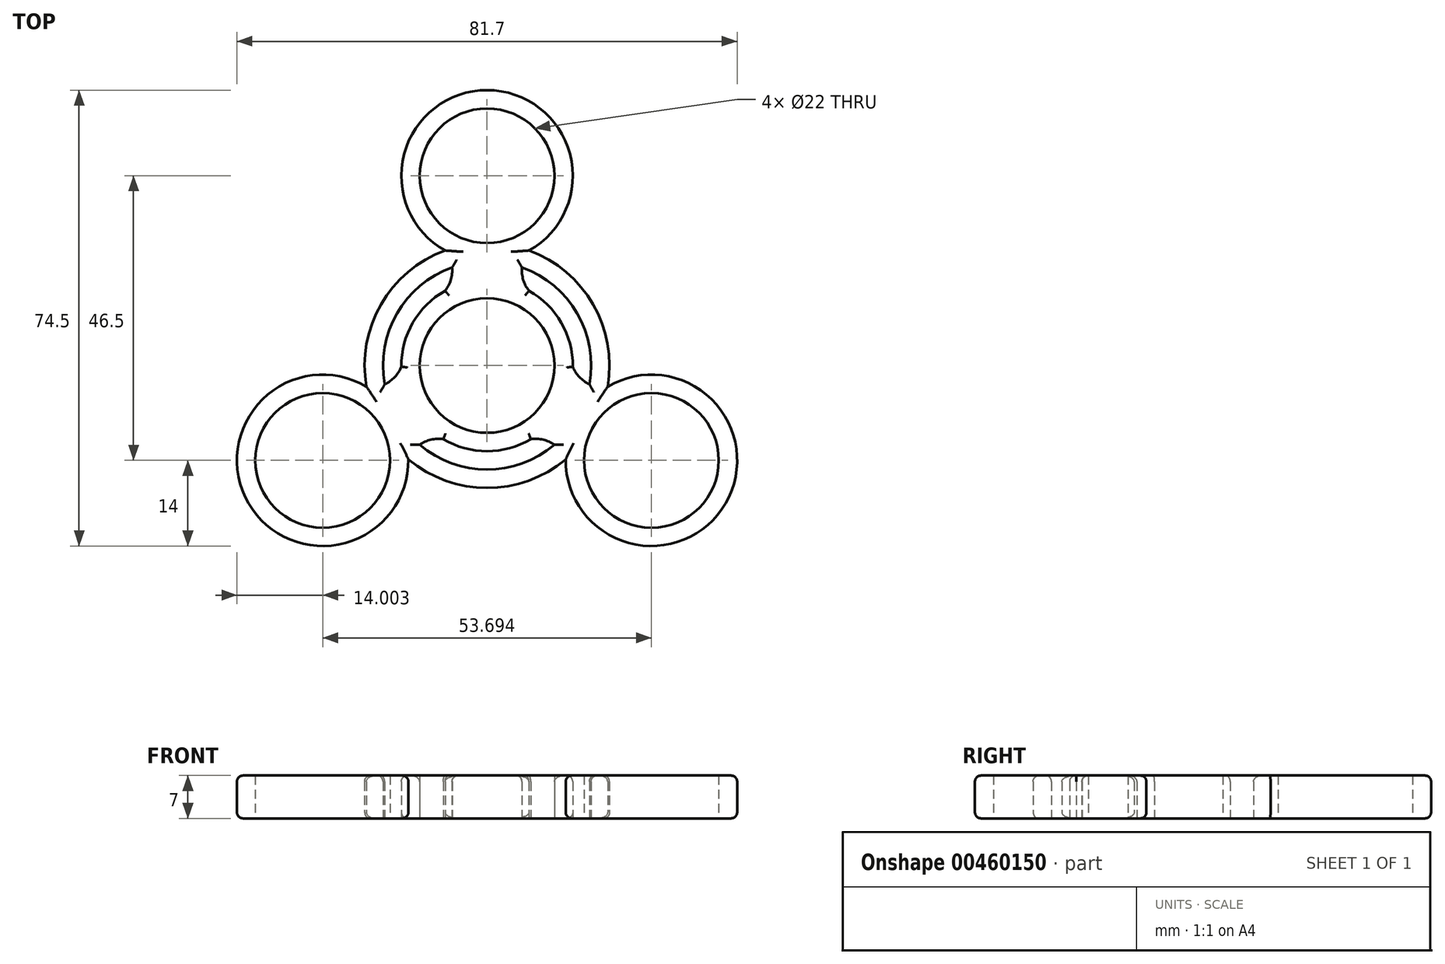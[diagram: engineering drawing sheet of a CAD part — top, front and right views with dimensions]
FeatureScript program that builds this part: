
annotation { "Feature Type Name" : "Feature", "Feature Type Description" : "" }
export const myFeature = defineFeature(function(context is Context, id is Id, definition is map)
    precondition{}
    {
        {
            var Q0;
            Q0=qCreatedBy(makeId("Top.planeOp"),FACE);
            var sketch = newSketch(context, id + "F0", { "sketchPlane" : qUnion([Q0])});
            skCircle(sketch, "E0", {"center": v(0, 0) * mm, "radius": 11 * mm});
            skArc(sketch, "E1.0", {"start": v(-6.85, 12.2) * mm, "mid": v(-12.12, -7) * mm, "end": v(7.15, -12.04) * mm});
            skCircle(sketch, "E2", {"center": v(0, 31) * mm, "radius": 11 * mm});
            skArc(sketch, "E3.0", {"start": v(6.85, 18.8) * mm, "mid": v(0, 45) * mm, "end": v(-6.85, 18.8) * mm});
            skPoint(sketch, "E4", {"position": v(0, 17) * mm});
            skArc(sketch, "E5", {"start": v(-5.72, 16.01) * mm, "mid": v(-14.72, 8.5) * mm, "end": v(-16.72, -3.05) * mm});
            skPoint(sketch, "E6", {"position": v(0, 20) * mm});
            skArc(sketch, "E7", {"start": v(-6.85, 18.8) * mm, "mid": v(-17.32, 10) * mm, "end": v(-19.7, -3.46) * mm});
            skArc(sketch, "E8", {"start": v(-6.85, 12.2) * mm, "mid": v(-5.91, 14) * mm, "end": v(-5.72, 16.01) * mm});
            skArc(sketch, "E9.MirrorCS", {"start": v(6.85, 12.2) * mm, "mid": v(5.91, 14) * mm, "end": v(5.72, 16.01) * mm});
            skCircle(sketch, "E10.1.0", {"center": v(-26.85, -15.5) * mm, "radius": 11 * mm});
            skArc(sketch, "E10.1.1", {"start": v(-19.7, -3.46) * mm, "mid": v(-38.97, -22.5) * mm, "end": v(-12.85, -15.33) * mm});
            skArc(sketch, "E10.1.2", {"start": v(-14, -0.17) * mm, "mid": v(-15.08, -1.88) * mm, "end": v(-16.72, -3.05) * mm});
            skArc(sketch, "E10.1.3", {"start": v(-7.15, -12.04) * mm, "mid": v(-9.17, -12.12) * mm, "end": v(-11, -12.96) * mm});
            skCircle(sketch, "E10.2.0", {"center": v(26.85, -15.5) * mm, "radius": 11 * mm});
            skArc(sketch, "E10.2.1", {"start": v(12.85, -15.33) * mm, "mid": v(38.97, -22.5) * mm, "end": v(19.7, -3.46) * mm});
            skArc(sketch, "E10.2.2", {"start": v(7.15, -12.04) * mm, "mid": v(9.17, -12.12) * mm, "end": v(11, -12.96) * mm});
            skArc(sketch, "E10.2.3", {"start": v(14, -0.17) * mm, "mid": v(15.08, -1.88) * mm, "end": v(16.72, -3.05) * mm});
            skPoint(sketch, "E11.orphan", {"position": v(6.85, 18.8) * mm});
            skArc(sketch, "E12.trimOffspring", {"start": v(16.72, -3.05) * mm, "mid": v(14.72, 8.5) * mm, "end": v(5.72, 16.01) * mm});
            skArc(sketch, "E13.trimOffspring", {"start": v(19.7, -3.46) * mm, "mid": v(17.32, 10) * mm, "end": v(6.85, 18.8) * mm});
            skArc(sketch, "E14.trimOffspring", {"start": v(-12.85, -15.33) * mm, "mid": v(0, -20) * mm, "end": v(12.85, -15.33) * mm});
            skArc(sketch, "E15.trimOffspring", {"start": v(-11, -12.96) * mm, "mid": v(0, -17) * mm, "end": v(11, -12.96) * mm});
            skArc(sketch, "E16.trimOffspring", {"start": v(14, -0.17) * mm, "mid": v(12.12, 7) * mm, "end": v(6.85, 12.2) * mm});
            skSolve(sketch);
        }
        {
            var Q0;
            Q0=makeQuery(id+"F0.imprint","IMPRINT",FACE,{"disambiguationData":[TD([[makeQuery(id+"F0.imprint","IMPRINT",EDGE,{"derivedFrom":sQuery(id+"F0.wireOp",EDGE,"E0")}),-1.0]])]});
            extrude(context, id + "F1", {"entities" : qUnion([Q0]), "depth" : 7 * mm});
        }
        {
            var Q0;
            Q0=makeQuery(id+"F1.opExtrude","CAP_EDGE",EDGE,{"disambiguationData":[OSD([sQuery(id+"F0.wireOp",EDGE,"E3.0")])],"isStart":false});
            var Q1;
            Q1=makeQuery(id+"F1.opExtrude","CAP_EDGE",EDGE,{"disambiguationData":[OSD([sQuery(id+"F0.wireOp",EDGE,"E7")])],"isStart":false});
            var Q2;
            Q2=makeQuery(id+"F1.opExtrude","CAP_EDGE",EDGE,{"disambiguationData":[OSD([sQuery(id+"F0.wireOp",EDGE,"E13.trimOffspring")])],"isStart":false});
            var Q3;
            Q3=makeQuery(id+"F1.opExtrude","CAP_EDGE",EDGE,{"disambiguationData":[OSD([sQuery(id+"F0.wireOp",EDGE,"E10.2.1")])],"isStart":false});
            var Q4;
            Q4=makeQuery(id+"F1.opExtrude","CAP_EDGE",EDGE,{"disambiguationData":[OSD([sQuery(id+"F0.wireOp",EDGE,"E14.trimOffspring")])],"isStart":false});
            var Q5;
            Q5=makeQuery(id+"F1.opExtrude","CAP_EDGE",EDGE,{"disambiguationData":[OSD([sQuery(id+"F0.wireOp",EDGE,"E10.1.1")])],"isStart":false});
            var Q6;
            Q6=makeQuery(id+"F1.opExtrude","CAP_EDGE",EDGE,{"disambiguationData":[OSD([sQuery(id+"F0.wireOp",EDGE,"E3.0")])],"isStart":true});
            var Q7;
            Q7=makeQuery(id+"F1.opExtrude","CAP_EDGE",EDGE,{"disambiguationData":[OSD([sQuery(id+"F0.wireOp",EDGE,"E7")])],"isStart":true});
            var Q8;
            Q8=makeQuery(id+"F1.opExtrude","CAP_EDGE",EDGE,{"disambiguationData":[OSD([sQuery(id+"F0.wireOp",EDGE,"E10.1.1")])],"isStart":true});
            var Q9;
            Q9=makeQuery(id+"F1.opExtrude","CAP_EDGE",EDGE,{"disambiguationData":[OSD([sQuery(id+"F0.wireOp",EDGE,"E14.trimOffspring")])],"isStart":true});
            var Q10;
            Q10=makeQuery(id+"F1.opExtrude","CAP_EDGE",EDGE,{"disambiguationData":[OSD([sQuery(id+"F0.wireOp",EDGE,"E13.trimOffspring")])],"isStart":true});
            var Q11;
            Q11=makeQuery(id+"F1.opExtrude","CAP_EDGE",EDGE,{"disambiguationData":[OSD([sQuery(id+"F0.wireOp",EDGE,"E10.2.1")])],"isStart":true});
            var Q12;
            Q12=makeQuery(id+"F1.opExtrude","CAP_EDGE",EDGE,{"disambiguationData":[OSD([sQuery(id+"F0.wireOp",EDGE,"E9.MirrorCS")])],"isStart":false});
            var Q13;
            Q13=makeQuery(id+"F1.opExtrude","CAP_EDGE",EDGE,{"disambiguationData":[OSD([sQuery(id+"F0.wireOp",EDGE,"E12.trimOffspring")])],"isStart":false});
            var Q14;
            Q14=makeQuery(id+"F1.opExtrude","CAP_EDGE",EDGE,{"disambiguationData":[OSD([sQuery(id+"F0.wireOp",EDGE,"E10.2.3")])],"isStart":false});
            var Q15;
            Q15=makeQuery(id+"F1.opExtrude","CAP_EDGE",EDGE,{"disambiguationData":[OSD([sQuery(id+"F0.wireOp",EDGE,"E16.trimOffspring")])],"isStart":false});
            var Q16;
            Q16=makeQuery(id+"F1.opExtrude","CAP_EDGE",EDGE,{"disambiguationData":[OSD([sQuery(id+"F0.wireOp",EDGE,"E8")])],"isStart":false});
            var Q17;
            Q17=makeQuery(id+"F1.opExtrude","CAP_EDGE",EDGE,{"disambiguationData":[OSD([sQuery(id+"F0.wireOp",EDGE,"E5")])],"isStart":false});
            var Q18;
            {var subQ0=sQuery(id+"F0.wireOp",EDGE,"E1.0");Q18=makeQuery(id+"F1.opExtrude","CAP_EDGE",EDGE,{"disambiguationData":[OSD([subQ0]),TDD([makeQuery(id+"F0.imprint","IMPRINT",EDGE,{"disambiguationData":[TD([[makeQuery(id+"F0.imprint","INTERSECT",VERTEX,{"derivedFrom":[subQ0,sQuery(id+"F0.wireOp",EDGE,"E8")]}),-1.0]])],"derivedFrom":subQ0})])],"isStart":false});}
            var Q19;
            Q19=makeQuery(id+"F1.opExtrude","CAP_EDGE",EDGE,{"disambiguationData":[OSD([sQuery(id+"F0.wireOp",EDGE,"E10.1.2")])],"isStart":false});
            var Q20;
            Q20=makeQuery(id+"F1.opExtrude","CAP_EDGE",EDGE,{"disambiguationData":[OSD([sQuery(id+"F0.wireOp",EDGE,"E15.trimOffspring")])],"isStart":false});
            var Q21;
            Q21=makeQuery(id+"F1.opExtrude","CAP_EDGE",EDGE,{"disambiguationData":[OSD([sQuery(id+"F0.wireOp",EDGE,"E10.1.3")])],"isStart":false});
            var Q22;
            {var subQ0=sQuery(id+"F0.wireOp",EDGE,"E1.0");Q22=makeQuery(id+"F1.opExtrude","CAP_EDGE",EDGE,{"disambiguationData":[OSD([subQ0]),TDD([makeQuery(id+"F0.imprint","IMPRINT",EDGE,{"disambiguationData":[TD([[makeQuery(id+"F0.imprint","INTERSECT",VERTEX,{"derivedFrom":[subQ0,sQuery(id+"F0.wireOp",EDGE,"E10.2.2")]}),1.0]])],"derivedFrom":subQ0})])],"isStart":false});}
            var Q23;
            Q23=makeQuery(id+"F1.opExtrude","CAP_EDGE",EDGE,{"disambiguationData":[OSD([sQuery(id+"F0.wireOp",EDGE,"E10.2.2")])],"isStart":false});
            fillet(context, id + "F2", {"entities" : qUnion([Q0, Q1, Q2, Q3, Q4, Q5, Q6, Q7, Q8, Q9, Q10, Q11, Q12, Q13, Q14, Q15, Q16, Q17, Q18, Q19, Q20, Q21, Q22, Q23]), "radius" : 1 * mm, "tangentPropagation" : true, "allowEdgeOverflow" : false});
        }
    });
